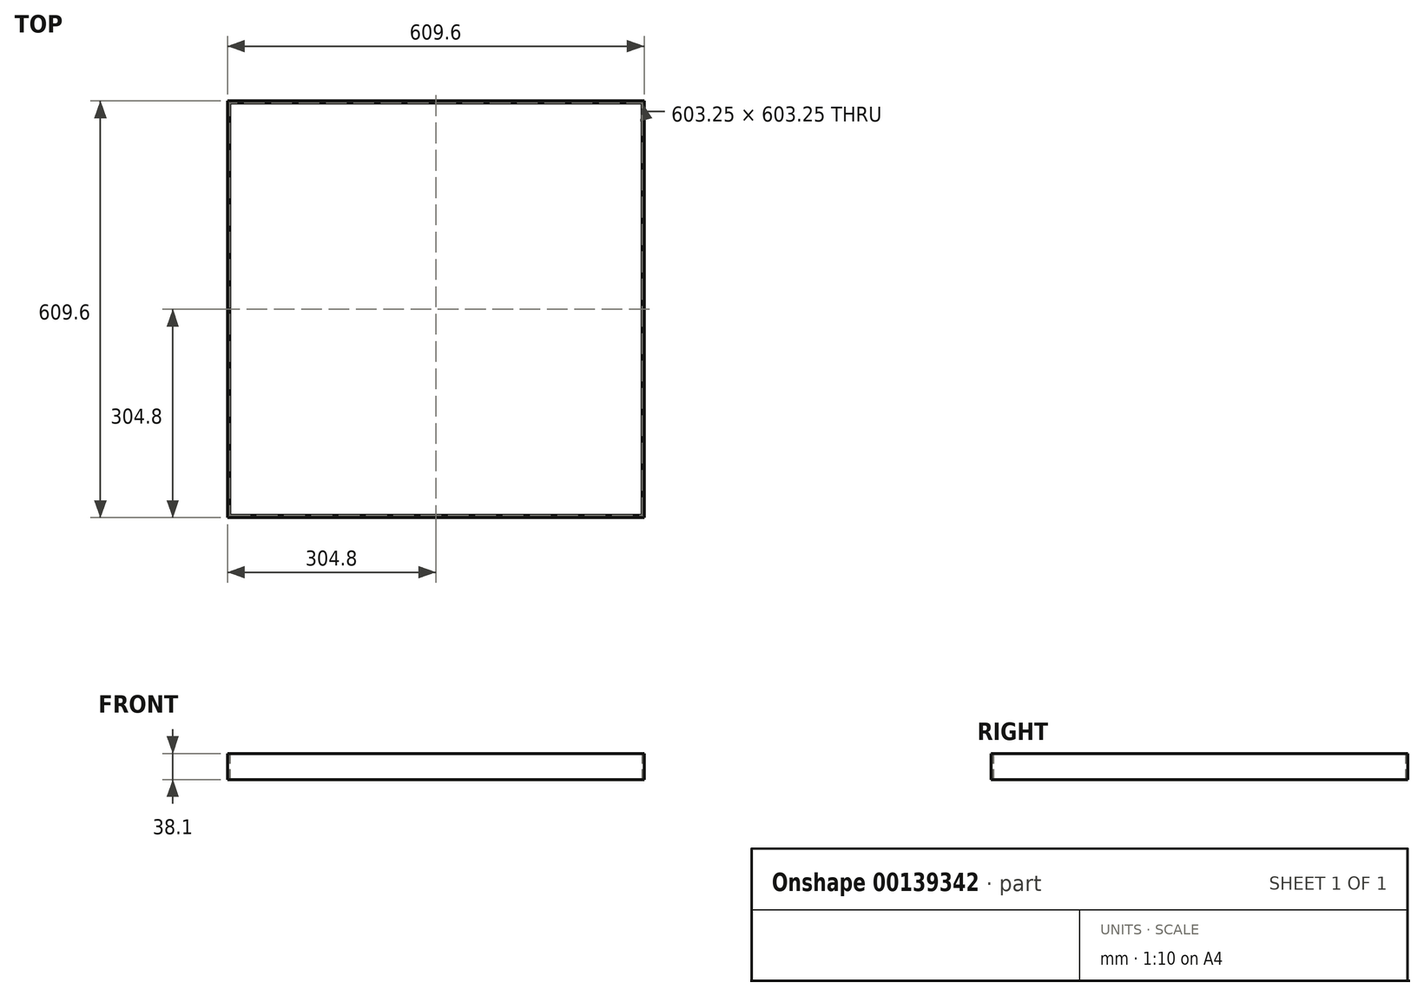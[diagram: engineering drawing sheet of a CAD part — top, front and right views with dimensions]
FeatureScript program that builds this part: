
annotation { "Feature Type Name" : "Feature", "Feature Type Description" : "" }
export const myFeature = defineFeature(function(context is Context, id is Id, definition is map)
    precondition{}
    {
        {
            var Q0;
            Q0=qCreatedBy(makeId("Top.planeOp"),FACE);
            var sketch = newSketch(context, id + "F0", { "sketchPlane" : qUnion([Q0])});
            skLineSegment(sketch, "E0.bottom", {"start": v(304.8, -304.8) * mm, "end": v(-304.8, -304.8) * mm});
            skLineSegment(sketch, "E0.top", {"start": v(304.8, 304.8) * mm, "end": v(-304.8, 304.8) * mm});
            skLineSegment(sketch, "E0.left", {"start": v(304.8, -304.8) * mm, "end": v(304.8, 304.8) * mm});
            skLineSegment(sketch, "E0.right", {"start": v(-304.8, -304.8) * mm, "end": v(-304.8, 304.8) * mm});
            skPoint(sketch, "E0.middle", {"position": v(0, 0) * mm});
            skLineSegment(sketch, "E1.bottom", {"start": v(266.7, -266.7) * mm, "end": v(-266.7, -266.7) * mm});
            skLineSegment(sketch, "E1.top", {"start": v(266.7, 266.7) * mm, "end": v(-266.7, 266.7) * mm});
            skLineSegment(sketch, "E1.left", {"start": v(266.7, -266.7) * mm, "end": v(266.7, 266.7) * mm});
            skLineSegment(sketch, "E1.right", {"start": v(-266.7, -266.7) * mm, "end": v(-266.7, 266.7) * mm});
            skLineSegment(sketch, "E2.bottom", {"start": v(301.62, -301.63) * mm, "end": v(-301.63, -301.63) * mm});
            skLineSegment(sketch, "E2.top", {"start": v(301.62, 301.63) * mm, "end": v(-301.63, 301.63) * mm});
            skLineSegment(sketch, "E2.left", {"start": v(301.62, -301.63) * mm, "end": v(301.62, 301.63) * mm});
            skLineSegment(sketch, "E2.right", {"start": v(-301.63, -301.63) * mm, "end": v(-301.63, 301.63) * mm});
            skSolve(sketch);
        }
        {
            var Q0;
            Q0=makeQuery(id+"F0.imprint","IMPRINT",FACE,{"disambiguationData":[TD([[makeQuery(id+"F0.imprint","IMPRINT",EDGE,{"derivedFrom":sQuery(id+"F0.wireOp",EDGE,"E0.bottom")}),-1.0]])]});
            extrude(context, id + "F1", {"entities" : qUnion([Q0]), "depth" : 38.1 * mm});
        }
    });
